# Revit family: Kabelrinnen-Systeme_Magic_Bogen_Variabel_Magic
name_source: partatom
category: Generic Models
revit_build: Autodesk Revit 2015 (Build: 20140606_1530(x64)
units: mm (PartAtom-declared; Revit-internal decimal feet)

## types (14) — shared parameters
Angle = 1.00°
Angle supp = 1.00°
Lenght 2 = 51 mm  [stored 0.167323 ft]
Manufacturer = OBO Bettermann
Material = Steel, Galvanized
URL = http://www.obo-bettermann.com

## per-type parameters (varying)
| type | B | GTIN | Lenght | Manufacturer Art. No. | Thickness |
| RBMV 610 FS | 100 mm  [stored 0.328084 ft] | 4012195992141 | 237 mm  [stored 0.777559 ft] | 6040480 | 1 mm  [stored 0.00328084 ft] |
| RBMV 615 FS | 150 mm | 4012195992158 | 317 mm  [stored 1.04003 ft] | 6040482 | 1 mm  [stored 0.00328084 ft] |
| RBMV 620 FS | 200 mm  [stored 0.656168 ft] | 4012195992165 | 387 mm  [stored 1.26969 ft] | 6040484 | 1 mm  [stored 0.00328084 ft] |
| RBMV 630 FS | 300 mm  [stored 0.984252 ft] | 4012195992172 | 537 mm  [stored 1.76181 ft] | 6040486 | 1 mm  [stored 0.00328084 ft] |
| RBMV 650 FS | 500 mm  [stored 1.64042 ft] | 4012195992196 | 857 mm  [stored 2.81168 ft] | 6040490 | 2 mm  [stored 0.00656168 ft] |
| RBMV 640 FT | 400 mm  [stored 1.31234 ft] | 4012195992257 | 717 mm  [stored 2.35236 ft] | 6040508 | 1 mm  [stored 0.00328084 ft] |
| RBMV 660 FS | 600 mm  [stored 1.9685 ft] | 4012195992202 | 1017 mm  [stored 3.33661 ft] | 6040492 | 2 mm  [stored 0.00656168 ft] |
| RBMV 610 FT | 100 mm  [stored 0.328084 ft] | 4012195992219 | 237 mm  [stored 0.777559 ft] | 6040500 | 1 mm  [stored 0.00328084 ft] |
| RBMV 615 FT | 150 mm | 4012195992226 | 317 mm  [stored 1.04003 ft] | 6040502 | 1 mm  [stored 0.00328084 ft] |
| RBMV 620 FT | 200 mm  [stored 0.656168 ft] | 4012195992233 | 387 mm  [stored 1.26969 ft] | 6040504 | 1 mm  [stored 0.00328084 ft] |
| RBMV 630 FT | 300 mm  [stored 0.984252 ft] | 4012195992240 | 500 mm  [stored 1.64042 ft] | 6040506 | 1 mm  [stored 0.00328084 ft] |
| RBMV 650 FT | 500 mm  [stored 1.64042 ft] | 4012195992264 | 857 mm  [stored 2.81168 ft] | 6040510 | 2 mm  [stored 0.00656168 ft] |
| RBMV 660 FT | 600 mm  [stored 1.9685 ft] | 4012195992271 | 1017 mm  [stored 3.33661 ft] | 6040512 | 2 mm  [stored 0.00656168 ft] |
| RBMV 640 FS | 400 mm  [stored 1.31234 ft] | 4012195992189 | 717 mm  [stored 2.35236 ft] | 6040488 | 1 mm  [stored 0.00328084 ft] |

note: column(s) folded — value = type name in every type: Article Type

note: [stored X ft] marks values corroborated as IEEE doubles in the binary element streams (Revit-internal decimal feet)

## geometry (parser evidence)
native form markers: Sweep x2
no freeform markers — native parametric forms only
